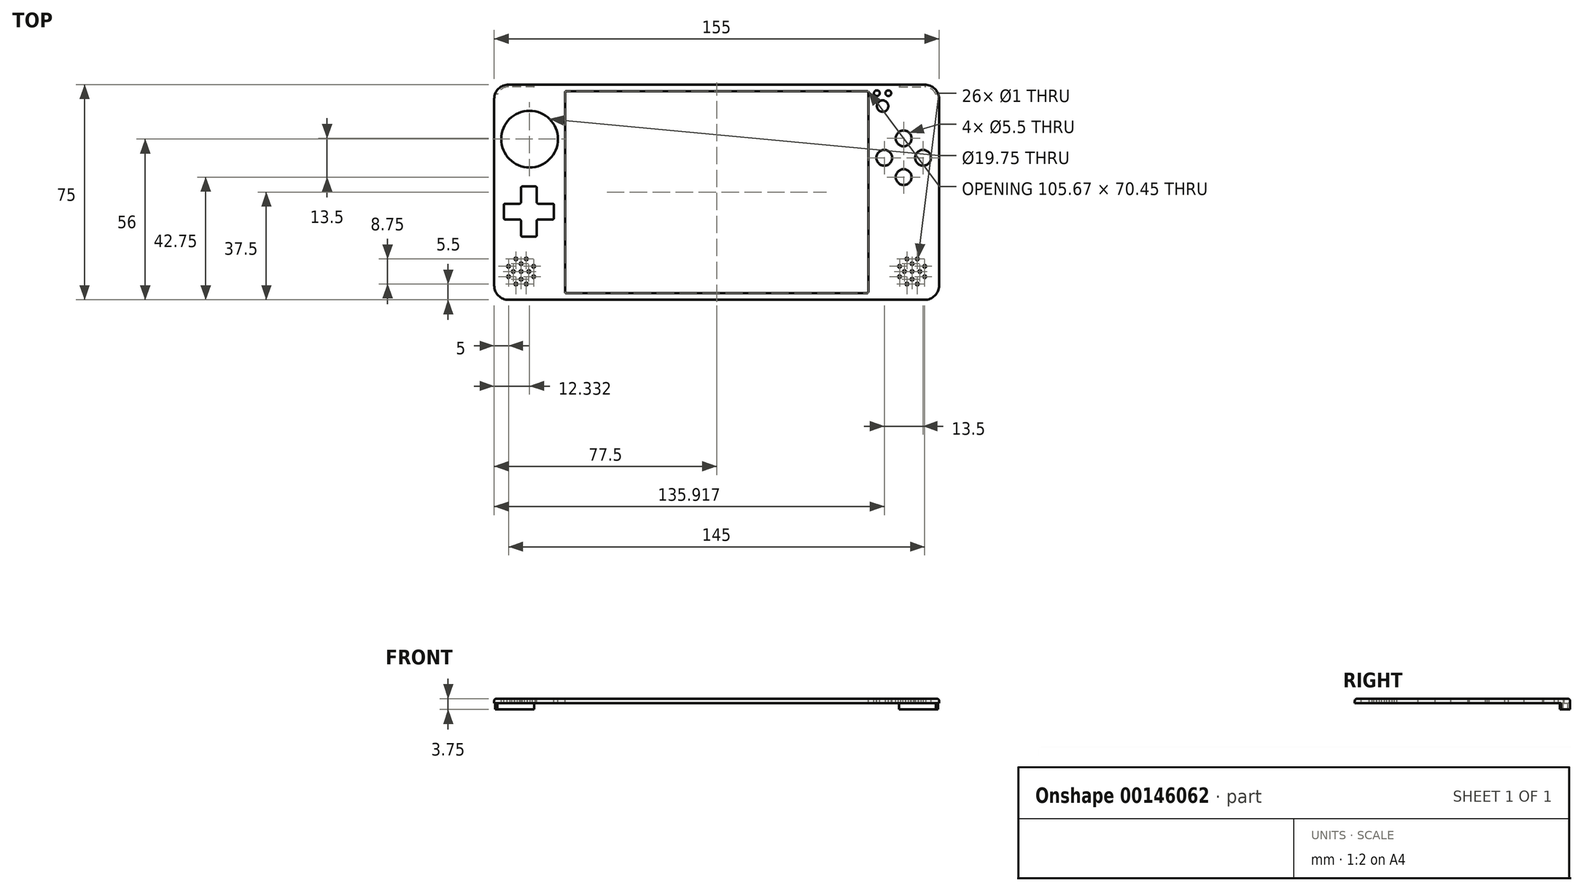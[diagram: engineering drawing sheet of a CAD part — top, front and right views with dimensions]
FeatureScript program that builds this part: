
annotation { "Feature Type Name" : "Feature", "Feature Type Description" : "" }
export const myFeature = defineFeature(function(context is Context, id is Id, definition is map)
    precondition{}
    {
        {
            var Q0;
            Q0=qCreatedBy(makeId("Top.planeOp"),FACE);
            var sketch = newSketch(context, id + "F0", { "sketchPlane" : qUnion([Q0])});
            skLineSegment(sketch, "E0.bottom", {"start": v(52.84, 35.22) * mm, "end": v(-52.84, 35.22) * mm});
            skLineSegment(sketch, "E0.top", {"start": v(52.84, -35.22) * mm, "end": v(-52.84, -35.22) * mm});
            skLineSegment(sketch, "E0.left", {"start": v(52.84, 35.22) * mm, "end": v(52.84, -35.22) * mm});
            skLineSegment(sketch, "E0.right", {"start": v(-52.84, 35.22) * mm, "end": v(-52.84, -35.22) * mm});
            skPoint(sketch, "E0.middle", {"position": v(0, 0) * mm});
            skLineSegment(sketch, "E1.bottom", {"start": v(72.5, 37.5) * mm, "end": v(-72.5, 37.5) * mm});
            skLineSegment(sketch, "E1.top", {"start": v(72.5, -37.5) * mm, "end": v(-72.5, -37.5) * mm});
            skLineSegment(sketch, "E1.left", {"start": v(77.5, 32.5) * mm, "end": v(77.5, -32.5) * mm});
            skLineSegment(sketch, "E1.right", {"start": v(-77.5, 32.5) * mm, "end": v(-77.5, -32.5) * mm});
            skPoint(sketch, "E2.visualSharp", {"position": v(-77.5, 37.5) * mm});
            skArc(sketch, "E2.filletArc", {"start": v(-72.5, 37.5) * mm, "mid": v(-76.04, 36.04) * mm, "end": v(-77.5, 32.5) * mm});
            skPoint(sketch, "E3.visualSharp", {"position": v(77.5, 37.5) * mm});
            skArc(sketch, "E3.filletArc", {"start": v(77.5, 32.5) * mm, "mid": v(76.04, 36.04) * mm, "end": v(72.5, 37.5) * mm});
            skPoint(sketch, "E4.visualSharp", {"position": v(77.5, -37.5) * mm});
            skArc(sketch, "E4.filletArc", {"start": v(72.5, -37.5) * mm, "mid": v(76.04, -36.04) * mm, "end": v(77.5, -32.5) * mm});
            skPoint(sketch, "E5.visualSharp", {"position": v(-77.5, -37.5) * mm});
            skArc(sketch, "E5.filletArc", {"start": v(-77.5, -32.5) * mm, "mid": v(-76.04, -36.04) * mm, "end": v(-72.5, -37.5) * mm});
            skCircle(sketch, "E6", {"center": v(-65.17, 18.5) * mm, "radius": 9.88 * mm});
            skLineSegment(sketch, "E7", {"start": v(-68.17, 2) * mm, "end": v(-62.67, 2) * mm});
            skLineSegment(sketch, "E8", {"start": v(-62.67, 2) * mm, "end": v(-62.67, -4) * mm});
            skLineSegment(sketch, "E9", {"start": v(-62.67, -4) * mm, "end": v(-56.67, -4) * mm});
            skLineSegment(sketch, "E10", {"start": v(-56.67, -4) * mm, "end": v(-56.67, -9.5) * mm});
            skLineSegment(sketch, "E11", {"start": v(-56.67, -9.5) * mm, "end": v(-62.67, -9.5) * mm});
            skLineSegment(sketch, "E12", {"start": v(-62.67, -9.5) * mm, "end": v(-62.67, -15.5) * mm});
            skLineSegment(sketch, "E13", {"start": v(-62.67, -15.5) * mm, "end": v(-68.17, -15.5) * mm});
            skLineSegment(sketch, "E14", {"start": v(-68.17, -15.5) * mm, "end": v(-68.17, -9.5) * mm});
            skLineSegment(sketch, "E15", {"start": v(-68.17, -9.5) * mm, "end": v(-74.17, -9.5) * mm});
            skLineSegment(sketch, "E16", {"start": v(-74.17, -9.5) * mm, "end": v(-74.17, -4) * mm});
            skLineSegment(sketch, "E17", {"start": v(-74.17, -4) * mm, "end": v(-68.17, -4) * mm});
            skLineSegment(sketch, "E18", {"start": v(-68.17, 2) * mm, "end": v(-68.17, -4) * mm});
            skLineSegment(sketch, "E19", {"start": v(-77.5, -7) * mm, "end": v(-52.84, -7) * mm, "construction": true});
            skLineSegment(sketch, "E20", {"start": v(-65.17, -7) * mm, "end": v(-65.17, 2) * mm, "construction": true});
            skLineSegment(sketch, "E21", {"start": v(65.17, 37.5) * mm, "end": v(65.17, 12) * mm, "construction": true});
            skLineSegment(sketch, "E22", {"start": v(71.92, 12) * mm, "end": v(58.42, 12) * mm, "construction": true});
            skLineSegment(sketch, "E23", {"start": v(65.17, 18.75) * mm, "end": v(65.17, 5.25) * mm, "construction": true});
            skCircle(sketch, "E24", {"center": v(71.92, 12) * mm, "radius": 2.75 * mm});
            skCircle(sketch, "E25", {"center": v(65.17, 18.75) * mm, "radius": 2.75 * mm});
            skCircle(sketch, "E26", {"center": v(58.42, 12) * mm, "radius": 2.75 * mm});
            skCircle(sketch, "E27", {"center": v(65.17, 5.25) * mm, "radius": 2.75 * mm});
            skCircle(sketch, "E28.cCircle", {"center": v(-68.12, -27.62) * mm, "radius": 4.38 * mm, "construction": true});
            skLineSegment(sketch, "E28.0", {"start": v(-72.5, -25.81) * mm, "end": v(-69.94, -23.25) * mm, "construction": true});
            skLineSegment(sketch, "E28.1", {"start": v(-69.94, -23.25) * mm, "end": v(-66.31, -23.25) * mm, "construction": true});
            skLineSegment(sketch, "E28.2", {"start": v(-66.31, -23.25) * mm, "end": v(-63.75, -25.81) * mm, "construction": true});
            skLineSegment(sketch, "E28.3", {"start": v(-63.75, -25.81) * mm, "end": v(-63.75, -29.44) * mm, "construction": true});
            skLineSegment(sketch, "E28.4", {"start": v(-63.75, -29.44) * mm, "end": v(-66.31, -32) * mm, "construction": true});
            skLineSegment(sketch, "E28.5", {"start": v(-66.31, -32) * mm, "end": v(-69.94, -32) * mm, "construction": true});
            skLineSegment(sketch, "E28.6", {"start": v(-69.94, -32) * mm, "end": v(-72.5, -29.44) * mm, "construction": true});
            skLineSegment(sketch, "E28.7", {"start": v(-72.5, -29.44) * mm, "end": v(-72.5, -25.81) * mm, "construction": true});
            skPoint(sketch, "E28.0.midPoint", {"position": v(-71.22, -24.53) * mm});
            skCircle(sketch, "E29", {"center": v(-69.94, -23.25) * mm, "radius": 0.5 * mm});
            skCircle(sketch, "E30", {"center": v(-66.31, -23.25) * mm, "radius": 0.5 * mm});
            skCircle(sketch, "E31", {"center": v(-63.75, -25.81) * mm, "radius": 0.5 * mm});
            skCircle(sketch, "E32", {"center": v(-63.75, -29.44) * mm, "radius": 0.5 * mm});
            skCircle(sketch, "E33", {"center": v(-66.31, -32) * mm, "radius": 0.5 * mm});
            skCircle(sketch, "E34", {"center": v(-69.94, -32) * mm, "radius": 0.5 * mm});
            skCircle(sketch, "E35", {"center": v(-72.5, -29.44) * mm, "radius": 0.5 * mm});
            skCircle(sketch, "E36", {"center": v(-72.5, -25.81) * mm, "radius": 0.5 * mm});
            skCircle(sketch, "E37", {"center": v(-68.12, -27.62) * mm, "radius": 0.5 * mm});
            skCircle(sketch, "E38", {"center": v(-68.12, -24.94) * mm, "radius": 0.5 * mm});
            skCircle(sketch, "E39", {"center": v(-70.81, -27.62) * mm, "radius": 0.5 * mm});
            skCircle(sketch, "E40", {"center": v(-68.12, -30.31) * mm, "radius": 0.5 * mm});
            skCircle(sketch, "E41", {"center": v(-65.44, -27.63) * mm, "radius": 0.5 * mm});
            skLineSegment(sketch, "E42", {"start": v(0, 0) * mm, "end": v(0, 9.85) * mm, "construction": true});
            skLineSegment(sketch, "E43", {"start": v(0.29, 0) * mm, "end": v(-9.18, 0) * mm, "construction": true});
            skCircle(sketch, "E44.MirrorC", {"center": v(66.31, -23.25) * mm, "radius": 0.5 * mm});
            skCircle(sketch, "E45.MirrorC", {"center": v(69.94, -23.25) * mm, "radius": 0.5 * mm});
            skCircle(sketch, "E46.MirrorC", {"center": v(72.5, -25.81) * mm, "radius": 0.5 * mm});
            skCircle(sketch, "E47.MirrorC", {"center": v(72.5, -29.44) * mm, "radius": 0.5 * mm});
            skCircle(sketch, "E48.MirrorC", {"center": v(69.94, -32) * mm, "radius": 0.5 * mm});
            skCircle(sketch, "E49.MirrorC", {"center": v(66.31, -32) * mm, "radius": 0.5 * mm});
            skCircle(sketch, "E50.MirrorC", {"center": v(63.75, -29.44) * mm, "radius": 0.5 * mm});
            skCircle(sketch, "E51.MirrorC", {"center": v(63.75, -25.81) * mm, "radius": 0.5 * mm});
            skCircle(sketch, "E52.MirrorC", {"center": v(68.12, -24.94) * mm, "radius": 0.5 * mm});
            skCircle(sketch, "E53.MirrorC", {"center": v(70.81, -27.62) * mm, "radius": 0.5 * mm});
            skCircle(sketch, "E54.MirrorC", {"center": v(68.12, -30.31) * mm, "radius": 0.5 * mm});
            skCircle(sketch, "E55.MirrorC", {"center": v(65.44, -27.63) * mm, "radius": 0.5 * mm});
            skCircle(sketch, "E56.MirrorC", {"center": v(68.12, -27.62) * mm, "radius": 0.5 * mm});
            skLineSegment(sketch, "E57", {"start": v(-68.12, -24.94) * mm, "end": v(-68.12, -30.31) * mm, "construction": true});
            skLineSegment(sketch, "E58", {"start": v(-70.81, -27.62) * mm, "end": v(-65.44, -27.62) * mm, "construction": true});
            skCircle(sketch, "E59", {"center": v(55.84, 34.5) * mm, "radius": 1 * mm});
            skCircle(sketch, "E60", {"center": v(57.84, 30) * mm, "radius": 2 * mm});
            skCircle(sketch, "E61", {"center": v(59.84, 34.5) * mm, "radius": 1 * mm});
            skSolve(sketch);
        }
        {
            var Q0;
            Q0=makeQuery(id+"F0.imprint","IMPRINT",FACE,{"disambiguationData":[TD([[makeQuery(id+"F0.imprint","IMPRINT",EDGE,{"derivedFrom":sQuery(id+"F0.wireOp",EDGE,"E0.bottom")}),-1.0]])]});
            extrude(context, id + "F1", {"entities" : qUnion([Q0]), "oppositeDirection" : true, "depth" : 1.5 * mm});
        }
        {
            var Q0;
            Q0=makeQuery(id+"F1.opExtrude","CAP_EDGE",EDGE,{"disambiguationData":[OSD([sQuery(id+"F0.wireOp",EDGE,"E1.top")])],"isStart":true});
            fillet(context, id + "F2", {"entities" : qUnion([Q0]), "radius" : 0.75 * mm, "tangentPropagation" : true, "allowEdgeOverflow" : false});
        }
        {
            var Q0;
            Q0=makeQuery(id+"F1.opExtrude","SWEPT_EDGE",EDGE,{"disambiguationData":[OSD([sQuery(id+"F0.wireOp",EDGE,"E0.bottom"),sQuery(id+"F0.wireOp",EDGE,"E0.right")])]});
            var Q1;
            Q1=makeQuery(id+"F1.opExtrude","SWEPT_EDGE",EDGE,{"disambiguationData":[OSD([sQuery(id+"F0.wireOp",EDGE,"E0.bottom"),sQuery(id+"F0.wireOp",EDGE,"E0.left")])]});
            var Q2;
            Q2=makeQuery(id+"F1.opExtrude","SWEPT_EDGE",EDGE,{"disambiguationData":[OSD([sQuery(id+"F0.wireOp",EDGE,"E0.top"),sQuery(id+"F0.wireOp",EDGE,"E0.right")])]});
            var Q3;
            Q3=makeQuery(id+"F1.opExtrude","SWEPT_EDGE",EDGE,{"disambiguationData":[OSD([sQuery(id+"F0.wireOp",EDGE,"E0.top"),sQuery(id+"F0.wireOp",EDGE,"E0.left")])]});
            fillet(context, id + "F3", {"entities" : qUnion([Q0, Q1, Q2, Q3]), "radius" : 0.5 * mm, "tangentPropagation" : true, "allowEdgeOverflow" : false});
        }
        {
            var Q0;
            Q0=makeQuery(id+"F1.opExtrude","SWEPT_EDGE",EDGE,{"disambiguationData":[OSD([sQuery(id+"F0.wireOp",EDGE,"E7"),sQuery(id+"F0.wireOp",EDGE,"E18")])]});
            var Q1;
            Q1=makeQuery(id+"F1.opExtrude","SWEPT_EDGE",EDGE,{"disambiguationData":[OSD([sQuery(id+"F0.wireOp",EDGE,"E17"),sQuery(id+"F0.wireOp",EDGE,"E18")])]});
            var Q2;
            Q2=makeQuery(id+"F1.opExtrude","SWEPT_EDGE",EDGE,{"disambiguationData":[OSD([sQuery(id+"F0.wireOp",EDGE,"E16"),sQuery(id+"F0.wireOp",EDGE,"E17")])]});
            var Q3;
            Q3=makeQuery(id+"F1.opExtrude","SWEPT_EDGE",EDGE,{"disambiguationData":[OSD([sQuery(id+"F0.wireOp",EDGE,"E8"),sQuery(id+"F0.wireOp",EDGE,"E9")])]});
            var Q4;
            Q4=makeQuery(id+"F1.opExtrude","SWEPT_EDGE",EDGE,{"disambiguationData":[OSD([sQuery(id+"F0.wireOp",EDGE,"E14"),sQuery(id+"F0.wireOp",EDGE,"E15")])]});
            var Q5;
            Q5=makeQuery(id+"F1.opExtrude","SWEPT_EDGE",EDGE,{"disambiguationData":[OSD([sQuery(id+"F0.wireOp",EDGE,"E12"),sQuery(id+"F0.wireOp",EDGE,"E13")])]});
            var Q6;
            Q6=makeQuery(id+"F1.opExtrude","SWEPT_EDGE",EDGE,{"disambiguationData":[OSD([sQuery(id+"F0.wireOp",EDGE,"E11"),sQuery(id+"F0.wireOp",EDGE,"E12")])]});
            var Q7;
            Q7=makeQuery(id+"F1.opExtrude","SWEPT_EDGE",EDGE,{"disambiguationData":[OSD([sQuery(id+"F0.wireOp",EDGE,"E10"),sQuery(id+"F0.wireOp",EDGE,"E11")])]});
            var Q8;
            Q8=makeQuery(id+"F1.opExtrude","SWEPT_EDGE",EDGE,{"disambiguationData":[OSD([sQuery(id+"F0.wireOp",EDGE,"E9"),sQuery(id+"F0.wireOp",EDGE,"E10")])]});
            var Q9;
            Q9=makeQuery(id+"F1.opExtrude","SWEPT_EDGE",EDGE,{"disambiguationData":[OSD([sQuery(id+"F0.wireOp",EDGE,"E7"),sQuery(id+"F0.wireOp",EDGE,"E8")])]});
            var Q10;
            Q10=makeQuery(id+"F1.opExtrude","SWEPT_EDGE",EDGE,{"disambiguationData":[OSD([sQuery(id+"F0.wireOp",EDGE,"E15"),sQuery(id+"F0.wireOp",EDGE,"E16")])]});
            var Q11;
            Q11=makeQuery(id+"F1.opExtrude","SWEPT_EDGE",EDGE,{"disambiguationData":[OSD([sQuery(id+"F0.wireOp",EDGE,"E13"),sQuery(id+"F0.wireOp",EDGE,"E14")])]});
            fillet(context, id + "F4", {"entities" : qUnion([Q0, Q1, Q2, Q3, Q4, Q5, Q6, Q7, Q8, Q9, Q10, Q11]), "radius" : 0.5 * mm, "tangentPropagation" : true, "allowEdgeOverflow" : false});
        }
        {
            var Q0;
            Q0=makeQuery(id+"F1.opExtrude","CAP_FACE",FACE,{"disambiguationData":[OSD([sQuery(id+"F0.wireOp",EDGE,"E0.bottom"),sQuery(id+"F0.wireOp",EDGE,"E0.top"),sQuery(id+"F0.wireOp",EDGE,"E0.left"),sQuery(id+"F0.wireOp",EDGE,"E0.right"),sQuery(id+"F0.wireOp",EDGE,"E1.bottom"),sQuery(id+"F0.wireOp",EDGE,"E1.top"),sQuery(id+"F0.wireOp",EDGE,"E1.left"),sQuery(id+"F0.wireOp",EDGE,"E1.right"),sQuery(id+"F0.wireOp",EDGE,"E2.filletArc"),sQuery(id+"F0.wireOp",EDGE,"E3.filletArc"),sQuery(id+"F0.wireOp",EDGE,"E4.filletArc"),sQuery(id+"F0.wireOp",EDGE,"E5.filletArc"),sQuery(id+"F0.wireOp",EDGE,"E6"),sQuery(id+"F0.wireOp",EDGE,"E7"),sQuery(id+"F0.wireOp",EDGE,"E8"),sQuery(id+"F0.wireOp",EDGE,"E9"),sQuery(id+"F0.wireOp",EDGE,"E10"),sQuery(id+"F0.wireOp",EDGE,"E11"),sQuery(id+"F0.wireOp",EDGE,"E12"),sQuery(id+"F0.wireOp",EDGE,"E13"),sQuery(id+"F0.wireOp",EDGE,"E14"),sQuery(id+"F0.wireOp",EDGE,"E15"),sQuery(id+"F0.wireOp",EDGE,"E16"),sQuery(id+"F0.wireOp",EDGE,"E17"),sQuery(id+"F0.wireOp",EDGE,"E18"),sQuery(id+"F0.wireOp",EDGE,"E24"),sQuery(id+"F0.wireOp",EDGE,"E25"),sQuery(id+"F0.wireOp",EDGE,"E26"),sQuery(id+"F0.wireOp",EDGE,"E27"),sQuery(id+"F0.wireOp",EDGE,"E29"),sQuery(id+"F0.wireOp",EDGE,"E30"),sQuery(id+"F0.wireOp",EDGE,"E31"),sQuery(id+"F0.wireOp",EDGE,"E32"),sQuery(id+"F0.wireOp",EDGE,"E33"),sQuery(id+"F0.wireOp",EDGE,"E34"),sQuery(id+"F0.wireOp",EDGE,"E35"),sQuery(id+"F0.wireOp",EDGE,"E36"),sQuery(id+"F0.wireOp",EDGE,"E37"),sQuery(id+"F0.wireOp",EDGE,"E38"),sQuery(id+"F0.wireOp",EDGE,"E39"),sQuery(id+"F0.wireOp",EDGE,"E40"),sQuery(id+"F0.wireOp",EDGE,"E41"),sQuery(id+"F0.wireOp",EDGE,"E44.MirrorC"),sQuery(id+"F0.wireOp",EDGE,"E45.MirrorC"),sQuery(id+"F0.wireOp",EDGE,"E46.MirrorC"),sQuery(id+"F0.wireOp",EDGE,"E47.MirrorC"),sQuery(id+"F0.wireOp",EDGE,"E48.MirrorC"),sQuery(id+"F0.wireOp",EDGE,"E49.MirrorC"),sQuery(id+"F0.wireOp",EDGE,"E50.MirrorC"),sQuery(id+"F0.wireOp",EDGE,"E51.MirrorC"),sQuery(id+"F0.wireOp",EDGE,"E52.MirrorC"),sQuery(id+"F0.wireOp",EDGE,"E53.MirrorC"),sQuery(id+"F0.wireOp",EDGE,"E54.MirrorC"),sQuery(id+"F0.wireOp",EDGE,"E55.MirrorC"),sQuery(id+"F0.wireOp",EDGE,"E56.MirrorC"),sQuery(id+"F0.wireOp",EDGE,"E59"),sQuery(id+"F0.wireOp",EDGE,"E60"),sQuery(id+"F0.wireOp",EDGE,"E61")])],"isStart":false});
            var sketch = newSketch(context, id + "F5", { "sketchPlane" : qUnion([Q0])});
            skLineSegment(sketch, "E62", {"start": v(72.5, -37.5) * mm, "end": v(63.75, -37.5) * mm});
            skLineSegment(sketch, "E63", {"start": v(63.75, -37.3) * mm, "end": v(63.75, -36.9) * mm});
            skLineSegment(sketch, "E64", {"start": v(63.75, -36.7) * mm, "end": v(72.5, -36.7) * mm});
            skLineSegment(sketch, "E65", {"start": v(72.5, -37.5) * mm, "end": v(72.5, -32.5) * mm});
            skLineSegment(sketch, "E66", {"start": v(72.5, -32.5) * mm, "end": v(77.5, -32.5) * mm});
            skArc(sketch, "E67", {"start": v(77.13, -34.38) * mm, "mid": v(77.4, -33.46) * mm, "end": v(77.5, -32.5) * mm});
            skArc(sketch, "E68", {"start": v(76.42, -34) * mm, "mid": v(76.63, -33.27) * mm, "end": v(76.7, -32.5) * mm});
            skLineSegment(sketch, "E69", {"start": v(75.79, -35.11) * mm, "end": v(76.41, -35.61) * mm});
            skArc(sketch, "E70", {"start": v(76.41, -35.61) * mm, "mid": v(76.35, -35.05) * mm, "end": v(75.79, -35.11) * mm});
            skLineSegment(sketch, "E71", {"start": v(76, -34.82) * mm, "end": v(76.67, -35.26) * mm});
            skPoint(sketch, "E72.orphan", {"position": v(76.35, -35.05) * mm});
            skLineSegment(sketch, "E73", {"start": v(76.5, -34.25) * mm, "end": v(76.84, -34.47) * mm});
            skArc(sketch, "E74.filletArc", {"start": v(76.84, -34.47) * mm, "mid": v(77, -34.5) * mm, "end": v(77.13, -34.38) * mm});
            skArc(sketch, "E75.filletArc", {"start": v(76.42, -34) * mm, "mid": v(76.42, -34.14) * mm, "end": v(76.5, -34.25) * mm});
            skArc(sketch, "E76", {"start": v(72.5, -37.5) * mm, "mid": v(74.67, -37) * mm, "end": v(76.41, -35.61) * mm});
            skArc(sketch, "E77", {"start": v(72.5, -36.7) * mm, "mid": v(74.88, -35.96) * mm, "end": v(76.42, -34) * mm});
            skArc(sketch, "E78", {"start": v(72.5, -36.7) * mm, "mid": v(74.32, -36.28) * mm, "end": v(75.79, -35.11) * mm});
            skArc(sketch, "E79", {"start": v(72.5, -37.5) * mm, "mid": v(75.3, -36.65) * mm, "end": v(77.13, -34.38) * mm});
            skLineSegment(sketch, "E80", {"start": v(0, 0) * mm, "end": v(0, -8.81) * mm, "construction": true});
            skLineSegment(sketch, "E81", {"start": v(63.55, -37.5) * mm, "end": v(63.35, -37.5) * mm});
            skLineSegment(sketch, "E82", {"start": v(63.55, -36.7) * mm, "end": v(63.35, -36.7) * mm});
            skPoint(sketch, "E83.visualSharp", {"position": v(63.75, -37.5) * mm});
            skArc(sketch, "E83.filletArc", {"start": v(63.55, -37.5) * mm, "mid": v(63.7, -37.44) * mm, "end": v(63.75, -37.3) * mm});
            skPoint(sketch, "E84.visualSharp", {"position": v(63.75, -36.7) * mm});
            skArc(sketch, "E84.filletArc", {"start": v(63.75, -36.9) * mm, "mid": v(63.7, -36.76) * mm, "end": v(63.55, -36.7) * mm});
            skLineSegment(sketch, "E85", {"start": v(63.55, -36.7) * mm, "end": v(63.75, -36.7) * mm});
            skLineSegment(sketch, "E86", {"start": v(63.55, -37.5) * mm, "end": v(63.75, -37.5) * mm});
            skArc(sketch, "E87.MirrorCS", {"start": v(-72.5, -37.5) * mm, "mid": v(-75.3, -36.65) * mm, "end": v(-77.13, -34.38) * mm});
            skLineSegment(sketch, "E88.MirrorCS", {"start": v(-72.5, -37.5) * mm, "end": v(-63.75, -37.5) * mm});
            skArc(sketch, "E89.MirrorCS", {"start": v(-76.84, -34.47) * mm, "mid": v(-77, -34.5) * mm, "end": v(-77.13, -34.38) * mm});
            skLineSegment(sketch, "E90.MirrorCS", {"start": v(-76.5, -34.25) * mm, "end": v(-76.84, -34.47) * mm});
            skArc(sketch, "E91.MirrorCS", {"start": v(-76.42, -34) * mm, "mid": v(-76.42, -34.14) * mm, "end": v(-76.5, -34.25) * mm});
            skArc(sketch, "E92.MirrorCS", {"start": v(-72.5, -36.7) * mm, "mid": v(-74.88, -35.96) * mm, "end": v(-76.42, -34) * mm});
            skLineSegment(sketch, "E93.MirrorCS", {"start": v(-63.75, -36.7) * mm, "end": v(-72.5, -36.7) * mm});
            skLineSegment(sketch, "E94.MirrorCS", {"start": v(-63.75, -37.3) * mm, "end": v(-63.75, -36.9) * mm});
            skArc(sketch, "E95.MirrorCS", {"start": v(-63.75, -36.9) * mm, "mid": v(-63.7, -36.76) * mm, "end": v(-63.55, -36.7) * mm});
            skLineSegment(sketch, "E96.MirrorCS", {"start": v(-63.55, -36.7) * mm, "end": v(-63.75, -36.7) * mm});
            skArc(sketch, "E97.MirrorCS", {"start": v(-63.55, -37.5) * mm, "mid": v(-63.7, -37.44) * mm, "end": v(-63.75, -37.3) * mm});
            skLineSegment(sketch, "E98.MirrorCS", {"start": v(-63.55, -37.5) * mm, "end": v(-63.75, -37.5) * mm});
            skSolve(sketch);
        }
        {
            var Q0;
            Q0=makeQuery(id+"F5.imprint","IMPRINT",FACE,{"disambiguationData":[TD([[makeQuery(id+"F5.imprint","IMPRINT",EDGE,{"derivedFrom":sQuery(id+"F5.wireOp",EDGE,"E87.MirrorCS")}),-1.0]])]});
            var Q1;
            {var subQ1=sQuery(id+"F5.wireOp",EDGE,"E62");Q1=makeQuery(id+"F5.imprint","IMPRINT",FACE,{"disambiguationData":[TD([[makeQuery(id+"F5.imprint","IMPRINT",EDGE,{"derivedFrom":subQ1}),-1.0]])]});}
            var Q2;
            {var subQ4=sQuery(id+"F5.wireOp",EDGE,"E69");Q2=makeQuery(id+"F5.imprint","IMPRINT",FACE,{"disambiguationData":[TD([[makeQuery(id+"F5.imprint","IMPRINT",EDGE,{"derivedFrom":subQ4}),-1.0]])]});}
            var Q3;
            {var subQ0=sQuery(id+"F5.wireOp",EDGE,"E69");Q3=makeQuery(id+"F5.imprint","IMPRINT",FACE,{"disambiguationData":[TD([[makeQuery(id+"F5.imprint","IMPRINT",EDGE,{"derivedFrom":subQ0}),1.0]])]});}
            var Q4;
            {var subQ0=sQuery(id+"F5.wireOp",EDGE,"E79");var subQ3=sQuery(id+"F5.wireOp",EDGE,"E71");var subQ5=makeQuery(id+"F5.imprint","INTERSECT",VERTEX,{"derivedFrom":[subQ3,subQ0]});Q4=makeQuery(id+"F5.imprint","IMPRINT",FACE,{"disambiguationData":[TD([[makeQuery(id+"F5.imprint","IMPRINT",EDGE,{"disambiguationData":[TD([[subQ5,1.0]])],"derivedFrom":subQ3}),-1.0]])]});}
            var Q5;
            Q5=makeQuery(id+"F5.imprint","IMPRINT",FACE,{"disambiguationData":[TD([[makeQuery(id+"F5.imprint","IMPRINT",EDGE,{"derivedFrom":sQuery(id+"F5.wireOp",EDGE,"E73")}),-1.0]])]});
            var Q6;
            {var subQ0=sQuery(id+"F5.wireOp",EDGE,"E77");var subQ3=sQuery(id+"F5.wireOp",EDGE,"E71");var subQ5=makeQuery(id+"F5.imprint","INTERSECT",VERTEX,{"derivedFrom":[subQ3,subQ0]});Q6=makeQuery(id+"F5.imprint","IMPRINT",FACE,{"disambiguationData":[TD([[makeQuery(id+"F5.imprint","IMPRINT",EDGE,{"disambiguationData":[TD([[subQ5,-1.0]])],"derivedFrom":subQ3}),-1.0]])]});}
            extrude(context, id + "F6", {"entities" : qUnion([Q0, Q1, Q2, Q3, Q4, Q5, Q6]), "operationType" : NewBodyOperationType.ADD, "depth" : 2.25 * mm});
        }
    });
